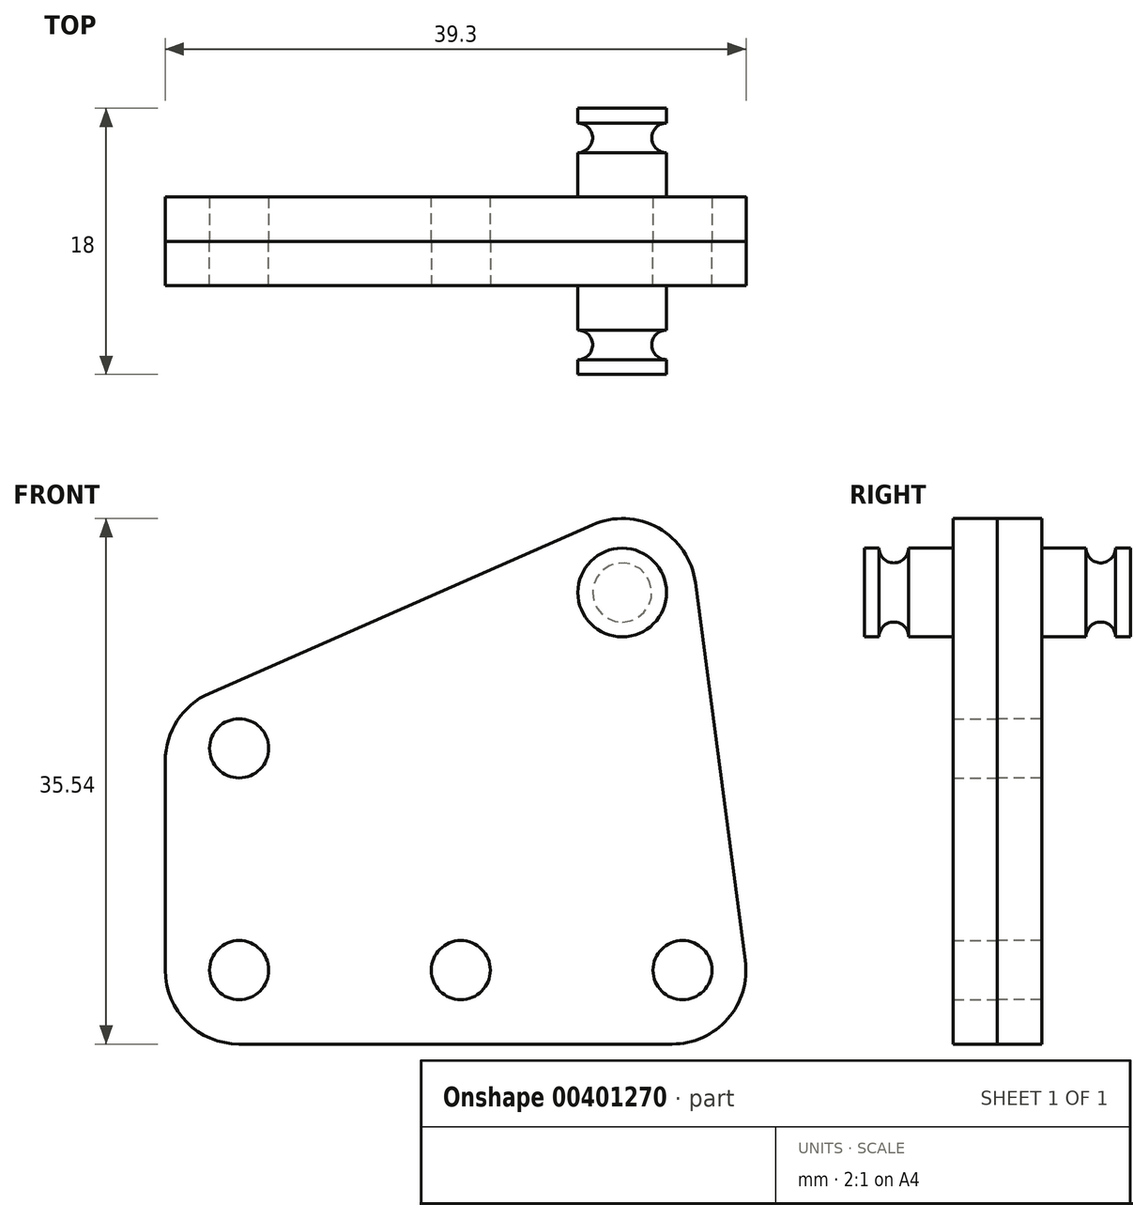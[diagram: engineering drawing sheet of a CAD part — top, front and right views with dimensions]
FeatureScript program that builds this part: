
annotation { "Feature Type Name" : "Feature", "Feature Type Description" : "" }
export const myFeature = defineFeature(function(context is Context, id is Id, definition is map)
    precondition{}
    {
        {
            var Q0;
            Q0=qCreatedBy(makeId("Front.planeOp"),FACE);
            var sketch = newSketch(context, id + "F0", { "sketchPlane" : qUnion([Q0])});
            skLineSegment(sketch, "E0.top", {"start": v(20, -20) * mm, "end": v(-20, -20) * mm});
            skLineSegment(sketch, "E0.right", {"start": v(-20, 2.4) * mm, "end": v(-20, -20) * mm});
            skPoint(sketch, "E0.middle", {"position": v(0, 0) * mm});
            skCircle(sketch, "E1", {"center": v(-15, 0) * mm, "radius": 2 * mm});
            skCircle(sketch, "E2", {"center": v(15, -15) * mm, "radius": 2 * mm});
            skLineSegment(sketch, "E3", {"start": v(-20, 2.4) * mm, "end": v(15, 17.8) * mm});
            skPoint(sketch, "E4.orphan", {"position": v(-20, 20) * mm});
            skLineSegment(sketch, "E5", {"start": v(15, -15) * mm, "end": v(15, 21.29) * mm, "construction": true});
            skLineSegment(sketch, "E6", {"start": v(15, 17.8) * mm, "end": v(20, -20) * mm});
            skPoint(sketch, "E7.orphan", {"position": v(20, 20) * mm});
            skSolve(sketch);
        }
        {
            var Q0;
            Q0 = qSketchRegion(id + "F0", true);
            extrude(context, id + "F1", {"entities" : qUnion([Q0]), "depth" : 3 * mm});
        }
        {
            var Q0;
            Q0=makeQuery(id+"F1.opExtrude","SWEPT_EDGE",EDGE,{"disambiguationData":[OSD([sQuery(id+"F0.wireOp",EDGE,"E3"),sQuery(id+"F0.wireOp",EDGE,"E6")])]});
            var Q1;
            Q1=makeQuery(id+"F1.opExtrude","SWEPT_EDGE",EDGE,{"disambiguationData":[OSD([sQuery(id+"F0.wireOp",EDGE,"E0.right"),sQuery(id+"F0.wireOp",EDGE,"E3")])]});
            var Q2;
            Q2=makeQuery(id+"F1.opExtrude","SWEPT_EDGE",EDGE,{"disambiguationData":[OSD([sQuery(id+"F0.wireOp",EDGE,"E0.top"),sQuery(id+"F0.wireOp",EDGE,"E6")])]});
            fillet(context, id + "F2", {"entities" : qUnion([Q0, Q1, Q2]), "radius" : 5 * mm, "tangentPropagation" : true, "allowEdgeOverflow" : false});
        }
        {
            var Q0;
            Q0=makeQuery(id+"F1.opExtrude","CAP_FACE",FACE,{"disambiguationData":[OSD([sQuery(id+"F0.wireOp",EDGE,"E0.top"),sQuery(id+"F0.wireOp",EDGE,"E0.right"),sQuery(id+"F0.wireOp",EDGE,"E1"),sQuery(id+"F0.wireOp",EDGE,"E2"),sQuery(id+"F0.wireOp",EDGE,"E3"),sQuery(id+"F0.wireOp",EDGE,"E6")])],"isStart":false});
            var sketch = newSketch(context, id + "F3", { "sketchPlane" : qUnion([Q0])});
            skCircle(sketch, "E8", {"center": v(10.92, 10.54) * mm, "radius": 3 * mm});
            skSolve(sketch);
        }
        {
            var Q0;
            Q0 = qSketchRegion(id + "F3", true);
            extrude(context, id + "F4", {"entities" : qUnion([Q0]), "operationType" : NewBodyOperationType.ADD, "depth" : 6 * mm});
        }
        {
            var Q0;
            Q0=makeQuery(id+"F4.opExtrude","CAP_EDGE",EDGE,{"disambiguationData":[OSD([sQuery(id+"F3.wireOp",EDGE,"E8")])],"isStart":false});
            cPlane(context, id + "F5", {"entities" : qUnion([Q0]), "cplaneType" : CPlaneType.LINE_ANGLE, "offset" : 25 * mm, "angle" : 0 * degree, "width" : 150 * mm, "height" : 150 * mm});
        }
        {
            var Q0;
            Q0=qCreatedBy(id+"F5.planeOp",FACE);
            var sketch = newSketch(context, id + "F6", { "sketchPlane" : qUnion([Q0])});
            skCircle(sketch, "E9", {"center": v(7.92, 7) * mm, "radius": 1 * mm});
            skSolve(sketch);
        }
        {
            var Q0;
            Q0=makeQuery(id+"F6.imprint","IMPRINT",FACE,{"disambiguationData":[TD([[makeQuery(id+"F6.imprint","IMPRINT",EDGE,{"derivedFrom":sQuery(id+"F6.wireOp",EDGE,"E9")}),1.0]])]});
            var Q1;
            Q1=makeQuery(id+"F4.opExtrude","CAP_EDGE",EDGE,{"disambiguationData":[OSD([sQuery(id+"F3.wireOp",EDGE,"E8")])],"isStart":false});
            revolve(context, id + "F7", {"operationType" : NewBodyOperationType.REMOVE, "entities" : qUnion([Q0]), "axis" : qUnion([Q1]), "revolveType" : RevolveType.FULL, "oppositeDirection" : true});
        }
        {
            var Q0;
            Q0=makeQuery(id+"F1.opExtrude","SWEPT_EDGE",EDGE,{"disambiguationData":[OSD([sQuery(id+"F0.wireOp",EDGE,"E0.top"),sQuery(id+"F0.wireOp",EDGE,"E0.right")])]});
            fillet(context, id + "F8", {"entities" : qUnion([Q0]), "radius" : 5 * mm, "tangentPropagation" : true, "allowEdgeOverflow" : false});
        }
        {
            var Q0;
            Q0=makeQuery(id+"F1.opExtrude","CAP_FACE",FACE,{"disambiguationData":[OSD([sQuery(id+"F0.wireOp",EDGE,"E0.top"),sQuery(id+"F0.wireOp",EDGE,"E0.right"),sQuery(id+"F0.wireOp",EDGE,"E1"),sQuery(id+"F0.wireOp",EDGE,"E2"),sQuery(id+"F0.wireOp",EDGE,"E3"),sQuery(id+"F0.wireOp",EDGE,"E6")])],"isStart":false});
            var sketch = newSketch(context, id + "F9", { "sketchPlane" : qUnion([Q0])});
            skCircle(sketch, "E10", {"center": v(-15, -15) * mm, "radius": 2 * mm});
            skCircle(sketch, "E11", {"center": v(0, -15) * mm, "radius": 2 * mm});
            skSolve(sketch);
        }
        {
            var Q0;
            Q0 = qSketchRegion(id + "F9", true);
            extrude(context, id + "F10", {"entities" : qUnion([Q0]), "operationType" : NewBodyOperationType.REMOVE, "oppositeDirection" : true, "depth" : 25 * mm});
        }
        {
            var Q0;
            Q0=makeQuery(id+"F1.opExtrude","SWEPT_BODY",BODY,{"disambiguationData":[OSD([sQuery(id+"F0.wireOp",EDGE,"E0.top"),sQuery(id+"F0.wireOp",EDGE,"E0.right"),sQuery(id+"F0.wireOp",EDGE,"E1"),sQuery(id+"F0.wireOp",EDGE,"E2"),sQuery(id+"F0.wireOp",EDGE,"E3"),sQuery(id+"F0.wireOp",EDGE,"E6")])]});
            var Q1;
            Q1=qCreatedBy(makeId("Front.planeOp"),FACE);
            mirror(context, id + "F11", {"entities" : qUnion([Q0]), "mirrorPlane" : qUnion([Q1])});
        }
    });
